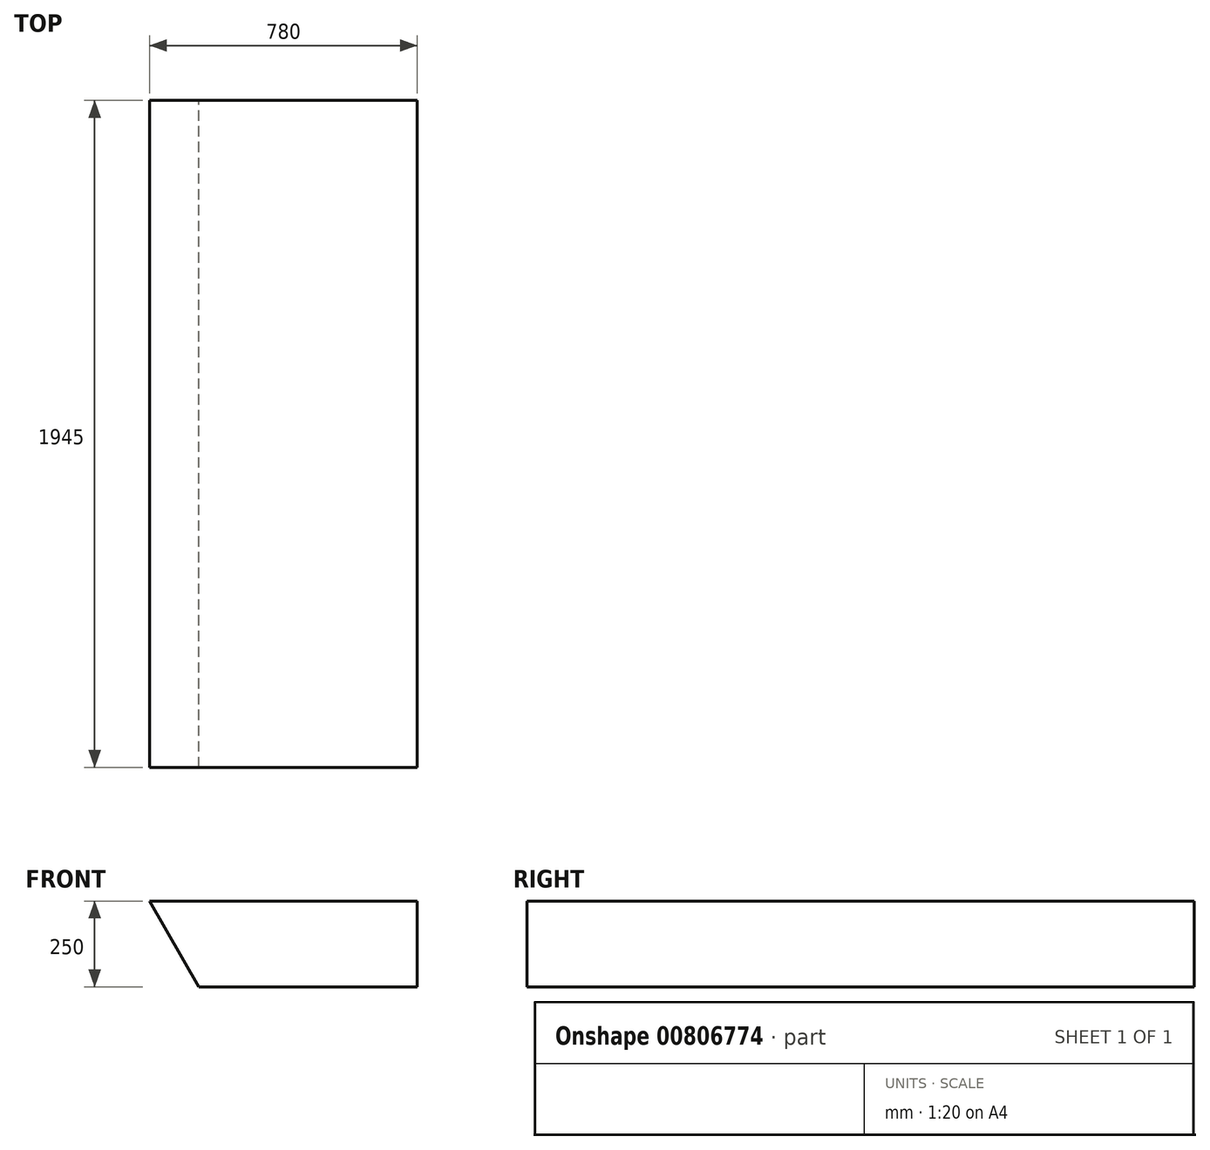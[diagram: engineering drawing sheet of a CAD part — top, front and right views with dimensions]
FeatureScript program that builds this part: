
annotation { "Feature Type Name" : "Feature", "Feature Type Description" : "" }
export const myFeature = defineFeature(function(context is Context, id is Id, definition is map)
    precondition{}
    {
        {
            var Q0;
            Q0=qCreatedBy(makeId("Front.planeOp"),FACE);
            var sketch = newSketch(context, id + "F0", { "sketchPlane" : qUnion([Q0])});
            skLineSegment(sketch, "E0", {"start": v(0, 0) * mm, "end": v(780, 0) * mm});
            skLineSegment(sketch, "E1", {"start": v(780, 0) * mm, "end": v(780, -250) * mm});
            skLineSegment(sketch, "E2", {"start": v(780, -250) * mm, "end": v(144.34, -250) * mm});
            skLineSegment(sketch, "E3", {"start": v(144.34, -250) * mm, "end": v(0, 0) * mm});
            skSolve(sketch);
        }
        {
            var Q0;
            Q0=makeQuery(id+"F0.imprint","IMPRINT",FACE,{"disambiguationData":[TD([[makeQuery(id+"F0.imprint","IMPRINT",EDGE,{"derivedFrom":sQuery(id+"F0.wireOp",EDGE,"E0")}),-1.0]])]});
            extrude(context, id + "F1", {"entities" : qUnion([Q0]), "depth" : 1945 * mm, "offsetDistance" : 25 * mm});
        }
    });
